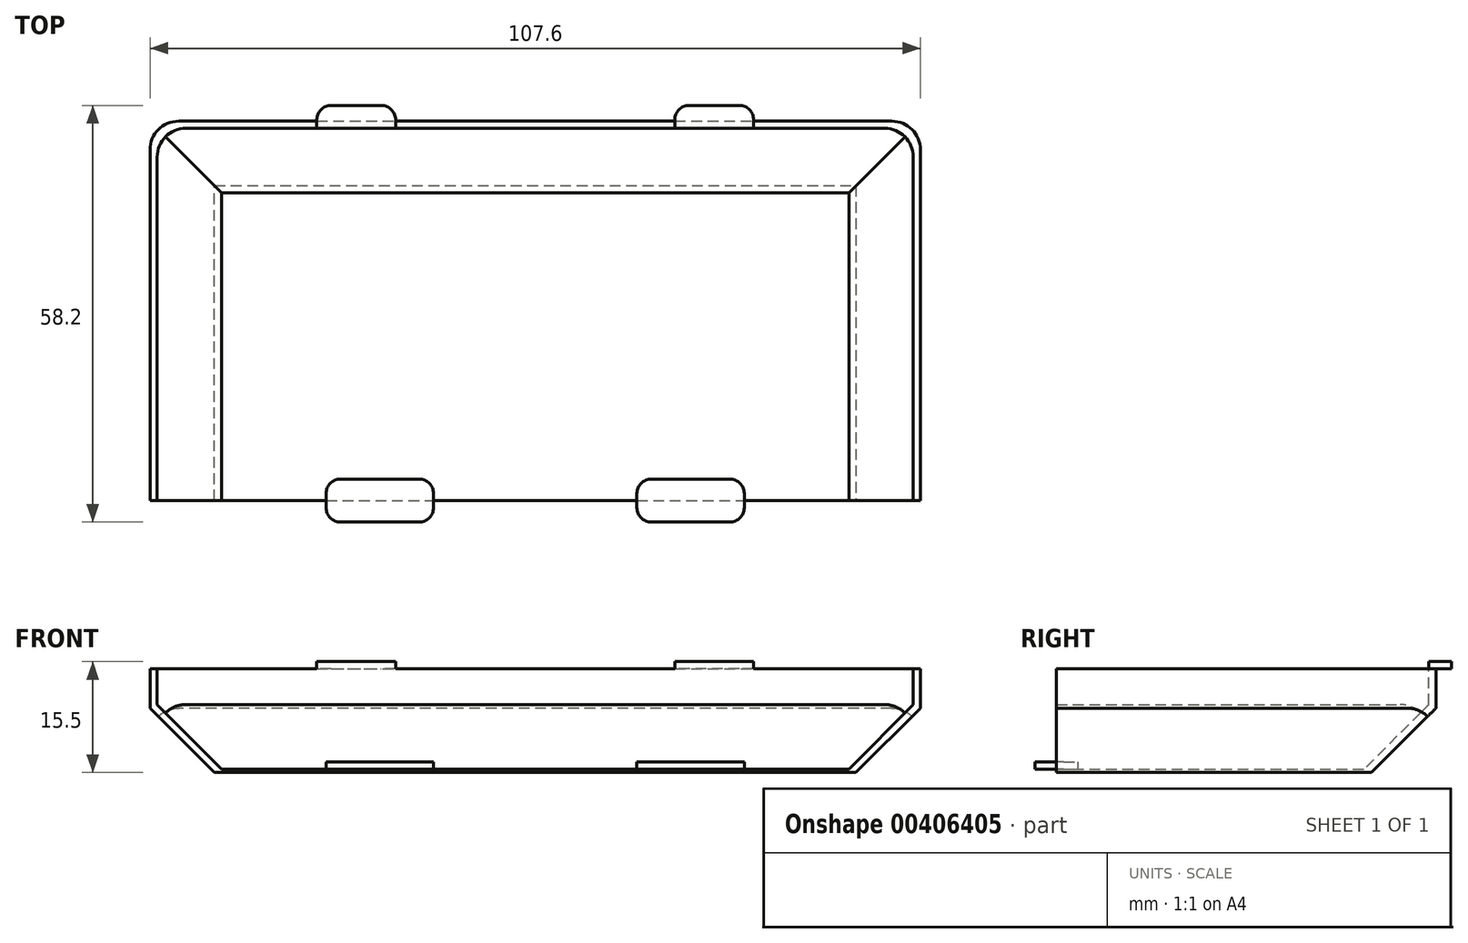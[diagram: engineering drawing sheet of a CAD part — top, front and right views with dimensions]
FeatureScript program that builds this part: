
annotation { "Feature Type Name" : "Feature", "Feature Type Description" : "" }
export const myFeature = defineFeature(function(context is Context, id is Id, definition is map)
    precondition{}
    {
        {
            var Q0;
            Q0=qCreatedBy(makeId("Top.planeOp"),FACE);
            var sketch = newSketch(context, id + "F0", { "sketchPlane" : qUnion([Q0])});
            skLineSegment(sketch, "E0.bottom", {"start": v(-53.8, 26.5) * mm, "end": v(53.8, 26.5) * mm});
            skLineSegment(sketch, "E0.top", {"start": v(-53.8, -26.5) * mm, "end": v(53.8, -26.5) * mm});
            skLineSegment(sketch, "E0.left", {"start": v(-53.8, 26.5) * mm, "end": v(-53.8, -26.5) * mm});
            skLineSegment(sketch, "E0.right", {"start": v(53.8, 26.5) * mm, "end": v(53.8, -26.5) * mm});
            skLineSegment(sketch, "E1", {"start": v(0, 26.5) * mm, "end": v(0, -26.5) * mm, "construction": true});
            skPoint(sketch, "E2", {"position": v(0, 0) * mm});
            skSolve(sketch);
        }
        {
            var Q0;
            Q0 = qSketchRegion(id + "F0", true);
            extrude(context, id + "F1", {"entities" : qUnion([Q0]), "depth" : 14.5 * mm});
        }
        {
            var Q0;
            Q0=makeQuery(id+"F1.opExtrude","CAP_FACE",FACE,{"disambiguationData":[OSD([sQuery(id+"F0.wireOp",EDGE,"E0.bottom"),sQuery(id+"F0.wireOp",EDGE,"E0.top"),sQuery(id+"F0.wireOp",EDGE,"E0.left"),sQuery(id+"F0.wireOp",EDGE,"E0.right")])],"isStart":false});
            var sketch = newSketch(context, id + "F2", { "sketchPlane" : qUnion([Q0])});
            skLineSegment(sketch, "E3.bottom", {"start": v(-52.8, -26.5) * mm, "end": v(52.8, -26.5) * mm});
            skLineSegment(sketch, "E3.top", {"start": v(-52.8, 25.5) * mm, "end": v(52.8, 25.5) * mm});
            skLineSegment(sketch, "E3.left", {"start": v(-52.8, -26.5) * mm, "end": v(-52.8, 25.5) * mm});
            skLineSegment(sketch, "E3.right", {"start": v(52.8, -26.5) * mm, "end": v(52.8, 25.5) * mm});
            skSolve(sketch);
        }
        {
            var Q0;
            Q0 = qSketchRegion(id + "F2", true);
            extrude(context, id + "F3", {"entities" : qUnion([Q0]), "operationType" : NewBodyOperationType.REMOVE, "oppositeDirection" : true, "depth" : 14 * mm});
        }
        {
            var Q0;
            Q0=makeQuery(id+"F1.opExtrude","CAP_EDGE",EDGE,{"disambiguationData":[OSD([sQuery(id+"F0.wireOp",EDGE,"E0.right")])],"isStart":true});
            var Q1;
            Q1=makeQuery(id+"F1.opExtrude","CAP_EDGE",EDGE,{"disambiguationData":[OSD([sQuery(id+"F0.wireOp",EDGE,"E0.bottom")])],"isStart":true});
            var Q2;
            Q2=makeQuery(id+"F1.opExtrude","CAP_EDGE",EDGE,{"disambiguationData":[OSD([sQuery(id+"F0.wireOp",EDGE,"E0.left")])],"isStart":true});
            var Q3;
            Q3=makeQuery(id+"F3.boolean.opBoolean","COPY",EDGE,{"derivedFrom":makeQuery(id+"F3.opExtrude","CAP_EDGE",EDGE,{"disambiguationData":[OSD([sQuery(id+"F2.wireOp",EDGE,"E3.left")])],"isStart":false})});
            var Q4;
            Q4=makeQuery(id+"F3.boolean.opBoolean","COPY",EDGE,{"derivedFrom":makeQuery(id+"F3.opExtrude","CAP_EDGE",EDGE,{"disambiguationData":[OSD([sQuery(id+"F2.wireOp",EDGE,"E3.top")])],"isStart":false})});
            var Q5;
            Q5=makeQuery(id+"F3.boolean.opBoolean","COPY",EDGE,{"derivedFrom":makeQuery(id+"F3.opExtrude","CAP_EDGE",EDGE,{"disambiguationData":[OSD([sQuery(id+"F2.wireOp",EDGE,"E3.right")])],"isStart":false})});
            chamfer(context, id + "F4", {"entities" : qUnion([Q0, Q1, Q2, Q3, Q4, Q5]), "width" : 9 * mm, "tangentPropagation" : true});
        }
        {
            var Q0;
            Q0=makeQuery(id+"F1.opExtrude","CAP_FACE",FACE,{"disambiguationData":[OSD([sQuery(id+"F0.wireOp",EDGE,"E0.bottom"),sQuery(id+"F0.wireOp",EDGE,"E0.top"),sQuery(id+"F0.wireOp",EDGE,"E0.left"),sQuery(id+"F0.wireOp",EDGE,"E0.right")])],"isStart":false});
            var sketch = newSketch(context, id + "F5", { "sketchPlane" : qUnion([Q0])});
            skLineSegment(sketch, "E4.bottom", {"start": v(-30.5, 25.5) * mm, "end": v(-19.5, 25.5) * mm});
            skLineSegment(sketch, "E4.top", {"start": v(-30.5, 28.7) * mm, "end": v(-19.5, 28.7) * mm});
            skLineSegment(sketch, "E4.left", {"start": v(-30.5, 25.5) * mm, "end": v(-30.5, 28.7) * mm});
            skLineSegment(sketch, "E4.right", {"start": v(-19.5, 25.5) * mm, "end": v(-19.5, 28.7) * mm});
            skLineSegment(sketch, "E5.MirrorCS", {"start": v(30.5, 25.5) * mm, "end": v(30.5, 28.7) * mm});
            skLineSegment(sketch, "E6.MirrorCS", {"start": v(19.5, 25.5) * mm, "end": v(19.5, 28.7) * mm});
            skLineSegment(sketch, "E7.MirrorCS", {"start": v(30.5, 28.7) * mm, "end": v(19.5, 28.7) * mm});
            skLineSegment(sketch, "E8.MirrorCS", {"start": v(30.5, 25.5) * mm, "end": v(19.5, 25.5) * mm});
            skSolve(sketch);
        }
        {
            var Q0;
            Q0 = qSketchRegion(id + "F5", true);
            extrude(context, id + "F6", {"entities" : qUnion([Q0]), "operationType" : NewBodyOperationType.ADD, "depth" : 1 * mm});
        }
        {
            var Q0;
            Q0=makeQuery(id+"F3.boolean.opBoolean","COPY",FACE,{"derivedFrom":makeQuery(id+"F3.opExtrude","CAP_FACE",FACE,{"disambiguationData":[OSD([sQuery(id+"F2.wireOp",EDGE,"E3.bottom"),sQuery(id+"F2.wireOp",EDGE,"E3.top"),sQuery(id+"F2.wireOp",EDGE,"E3.left"),sQuery(id+"F2.wireOp",EDGE,"E3.right")])],"isStart":false})});
            var sketch = newSketch(context, id + "F7", { "sketchPlane" : qUnion([Q0])});
            skLineSegment(sketch, "E9.bottom", {"start": v(-29.2, -23.5) * mm, "end": v(-14.2, -23.5) * mm});
            skLineSegment(sketch, "E9.top", {"start": v(-29.2, -29.5) * mm, "end": v(-14.2, -29.5) * mm});
            skLineSegment(sketch, "E9.left", {"start": v(-14.2, -23.5) * mm, "end": v(-14.2, -29.5) * mm});
            skLineSegment(sketch, "E9.right", {"start": v(-29.2, -23.5) * mm, "end": v(-29.2, -29.5) * mm});
            skLineSegment(sketch, "E10.MirrorCS", {"start": v(29.2, -29.5) * mm, "end": v(14.2, -29.5) * mm});
            skLineSegment(sketch, "E11.MirrorCS", {"start": v(29.2, -23.5) * mm, "end": v(14.2, -23.5) * mm});
            skLineSegment(sketch, "E12.MirrorCS", {"start": v(14.2, -23.5) * mm, "end": v(14.2, -29.5) * mm});
            skLineSegment(sketch, "E13.MirrorCS", {"start": v(29.2, -23.5) * mm, "end": v(29.2, -29.5) * mm});
            skSolve(sketch);
        }
        {
            var Q0;
            Q0 = qSketchRegion(id + "F7", true);
            extrude(context, id + "F8", {"entities" : qUnion([Q0]), "operationType" : NewBodyOperationType.ADD, "depth" : 1 * mm});
        }
        {
            var Q0;
            Q0=makeQuery(id+"F8.opExtrude","SWEPT_EDGE",EDGE,{"disambiguationData":[OSD([sQuery(id+"F7.wireOp",EDGE,"E9.top"),sQuery(id+"F7.wireOp",EDGE,"E9.right")])]});
            var Q1;
            Q1=makeQuery(id+"F8.opExtrude","SWEPT_EDGE",EDGE,{"disambiguationData":[OSD([sQuery(id+"F7.wireOp",EDGE,"E9.top"),sQuery(id+"F7.wireOp",EDGE,"E9.left")])]});
            var Q2;
            Q2=makeQuery(id+"F8.opExtrude","SWEPT_EDGE",EDGE,{"disambiguationData":[OSD([sQuery(id+"F7.wireOp",EDGE,"E10.MirrorCS"),sQuery(id+"F7.wireOp",EDGE,"E12.MirrorCS")])]});
            var Q3;
            Q3=makeQuery(id+"F8.opExtrude","SWEPT_EDGE",EDGE,{"disambiguationData":[OSD([sQuery(id+"F7.wireOp",EDGE,"E10.MirrorCS"),sQuery(id+"F7.wireOp",EDGE,"E13.MirrorCS")])]});
            var Q4;
            Q4=makeQuery(id+"F8.opExtrude","SWEPT_EDGE",EDGE,{"disambiguationData":[OSD([sQuery(id+"F7.wireOp",EDGE,"E11.MirrorCS"),sQuery(id+"F7.wireOp",EDGE,"E13.MirrorCS")])]});
            var Q5;
            Q5=makeQuery(id+"F8.opExtrude","SWEPT_EDGE",EDGE,{"disambiguationData":[OSD([sQuery(id+"F7.wireOp",EDGE,"E11.MirrorCS"),sQuery(id+"F7.wireOp",EDGE,"E12.MirrorCS")])]});
            var Q6;
            Q6=makeQuery(id+"F8.opExtrude","SWEPT_EDGE",EDGE,{"disambiguationData":[OSD([sQuery(id+"F7.wireOp",EDGE,"E9.bottom"),sQuery(id+"F7.wireOp",EDGE,"E9.right")])]});
            var Q7;
            Q7=makeQuery(id+"F8.opExtrude","SWEPT_EDGE",EDGE,{"disambiguationData":[OSD([sQuery(id+"F7.wireOp",EDGE,"E9.bottom"),sQuery(id+"F7.wireOp",EDGE,"E9.left")])]});
            var Q8;
            Q8=makeQuery(id+"F6.opExtrude","SWEPT_EDGE",EDGE,{"disambiguationData":[OSD([sQuery(id+"F5.wireOp",EDGE,"E5.MirrorCS"),sQuery(id+"F5.wireOp",EDGE,"E7.MirrorCS")])]});
            var Q9;
            Q9=makeQuery(id+"F6.opExtrude","SWEPT_EDGE",EDGE,{"disambiguationData":[OSD([sQuery(id+"F5.wireOp",EDGE,"E6.MirrorCS"),sQuery(id+"F5.wireOp",EDGE,"E7.MirrorCS")])]});
            var Q10;
            Q10=makeQuery(id+"F6.opExtrude","SWEPT_EDGE",EDGE,{"disambiguationData":[OSD([sQuery(id+"F5.wireOp",EDGE,"E4.top"),sQuery(id+"F5.wireOp",EDGE,"E4.right")])]});
            var Q11;
            Q11=makeQuery(id+"F6.opExtrude","SWEPT_EDGE",EDGE,{"disambiguationData":[OSD([sQuery(id+"F5.wireOp",EDGE,"E4.top"),sQuery(id+"F5.wireOp",EDGE,"E4.left")])]});
            fillet(context, id + "F9", {"entities" : qUnion([Q0, Q1, Q2, Q3, Q4, Q5, Q6, Q7, Q8, Q9, Q10, Q11]), "radius" : 2 * mm, "tangentPropagation" : true, "allowEdgeOverflow" : false});
        }
        {
            var Q0;
            Q0=makeQuery(id+"F1.opExtrude","SWEPT_EDGE",EDGE,{"disambiguationData":[OSD([sQuery(id+"F0.wireOp",EDGE,"E0.bottom"),sQuery(id+"F0.wireOp",EDGE,"E0.right")])]});
            var Q1;
            Q1=makeQuery(id+"F3.boolean.opBoolean","COPY",EDGE,{"derivedFrom":makeQuery(id+"F3.opExtrude","SWEPT_EDGE",EDGE,{"disambiguationData":[OSD([sQuery(id+"F2.wireOp",EDGE,"E3.top"),sQuery(id+"F2.wireOp",EDGE,"E3.right")])]})});
            var Q2;
            Q2=makeQuery(id+"F3.boolean.opBoolean","COPY",EDGE,{"derivedFrom":makeQuery(id+"F3.opExtrude","SWEPT_EDGE",EDGE,{"disambiguationData":[OSD([sQuery(id+"F2.wireOp",EDGE,"E3.top"),sQuery(id+"F2.wireOp",EDGE,"E3.left")])]})});
            var Q3;
            Q3=makeQuery(id+"F1.opExtrude","SWEPT_EDGE",EDGE,{"disambiguationData":[OSD([sQuery(id+"F0.wireOp",EDGE,"E0.bottom"),sQuery(id+"F0.wireOp",EDGE,"E0.left")])]});
            fillet(context, id + "F10", {"entities" : qUnion([Q0, Q1, Q2, Q3]), "radius" : 4 * mm, "tangentPropagation" : true, "allowEdgeOverflow" : false});
        }
    });
